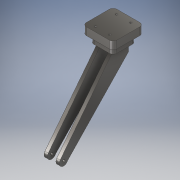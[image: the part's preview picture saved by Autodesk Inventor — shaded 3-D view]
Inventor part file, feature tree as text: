
AUTODESK INVENTOR PART (.ipt)
format: ipt  version: 2018 (Build 220112000, 112)  size: 182,272 bytes
history: native  units: in
note: dims shown in document units (in); Inventor stores cm internally (conversion verified against a paired STEP export)
features: extrude x5, sketch x5, plane x1, mirror x1
ambient origin geometry x8: Origin, YZ Plane, XZ Plane, XY Plane, X Axis, Y Axis, Z Axis, Center Point
bodies: Solid1 (feature_tree)
feature tree (12):
  extrude  "Extrusion1"  Depth=6.2992in
  extrude  "Extrusion2"  Depth=1.5748in TaperAngle=0.0deg
  extrude  "Extrusion3"  Depth=1.4764in
  plane  "Work Plane1"
  extrude  "Extrusion4"  Depth=1.4764in
  mirror  "Mirror1"
  extrude  "Extrusion5"  Depth=0.3937in
  sketch  "Sketch1"  dims[d0=6.2992in d1=6.2992in]
  sketch  "Sketch2"  dims[d2=0.7874in d3=1.5748in d4=0.0in]
  sketch  "Sketch3"  dims[d9=1.5748in d10=0.0in d15=1.4764in]
  sketch  "Sketch4"  dims[d16=1.4764in d17=2.1654in]
  sketch  "Sketch5"  dims[d18=0.2362in d19=0.0in d20=0.3937in d21=0.3937in d23=2.3622in d25=2.3622in d26=0.7874in d27=1.5748in d28=1.7717in d29=23.622in d30=17.7165in d31=11.811in d33=0.689in d34=0.0in d35=0.5906in d36=0.3937in d37=0.0in]
